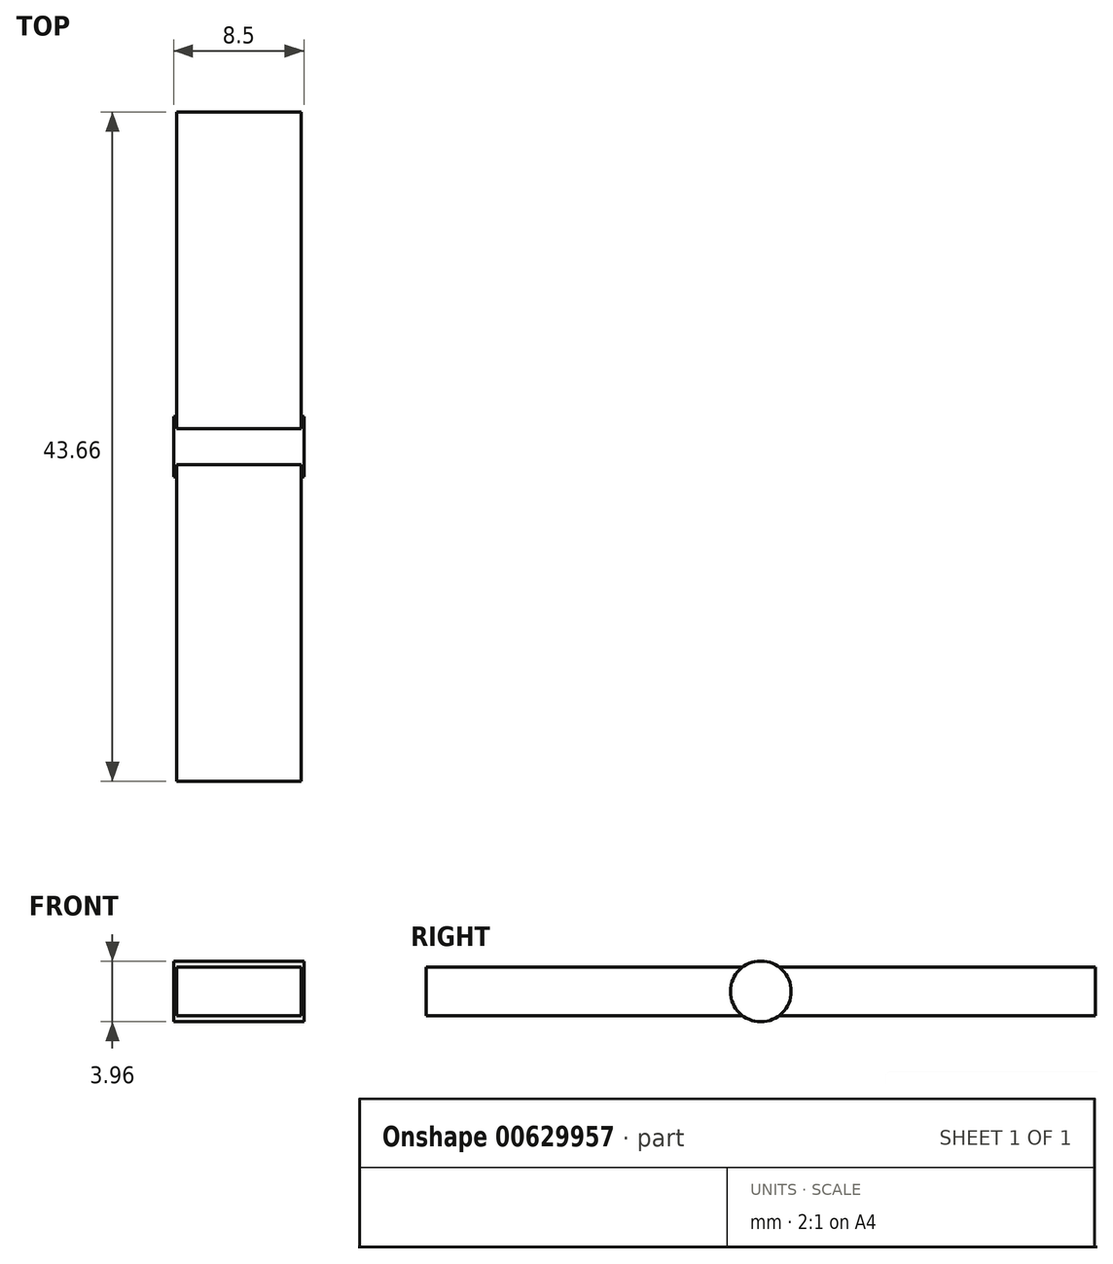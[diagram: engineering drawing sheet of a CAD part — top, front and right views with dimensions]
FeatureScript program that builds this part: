
annotation { "Feature Type Name" : "Feature", "Feature Type Description" : "" }
export const myFeature = defineFeature(function(context is Context, id is Id, definition is map)
    precondition{}
    {
        {
            assignVariable(context, id + "F0", {"name" : "SlatLength", "anyValue" : 8.12});
        }
        {
            var Q0;
            Q0=qCreatedBy(makeId("Right.planeOp"),FACE);
            var sketch = newSketch(context, id + "F1", { "sketchPlane" : qUnion([Q0])});
            skLineSegment(sketch, "E0.bottom", {"start": v(21.83, 1.59) * mm, "end": v(-21.83, 1.59) * mm});
            skLineSegment(sketch, "E0.top", {"start": v(21.83, -1.59) * mm, "end": v(-21.83, -1.59) * mm});
            skLineSegment(sketch, "E0.left", {"start": v(21.83, 1.59) * mm, "end": v(21.83, -1.59) * mm});
            skLineSegment(sketch, "E0.right", {"start": v(-21.83, 1.59) * mm, "end": v(-21.83, -1.59) * mm});
            skPoint(sketch, "E0.middle", {"position": v(0, 0) * mm});
            skSolve(sketch);
        }
        {
            var Q0;
            Q0 = qSketchRegion(id + "F1", true);
            extrude(context, id + "F2", {"entities" : qUnion([Q0]), "endBound" : BoundingType.SYMMETRIC, "depth" : (getVariable(context, 'SlatLength')) * mm, "offsetDistance" : 25.4 * mm});
        }
        {
            var Q0;
            Q0=qCreatedBy(makeId("Right.planeOp"),FACE);
            var sketch = newSketch(context, id + "F3", { "sketchPlane" : qUnion([Q0])});
            skCircle(sketch, "E1", {"center": v(0, 0) * mm, "radius": 1.98 * mm});
            skSolve(sketch);
        }
        {
            var Q0;
            Q0 = qSketchRegion(id + "F3", true);
            extrude(context, id + "F4", {"entities" : qUnion([Q0]), "operationType" : NewBodyOperationType.ADD, "endBound" : BoundingType.SYMMETRIC, "depth" : (getVariable(context, 'SlatLength') + .375) * mm, "offsetDistance" : 25.4 * mm});
        }
    });
